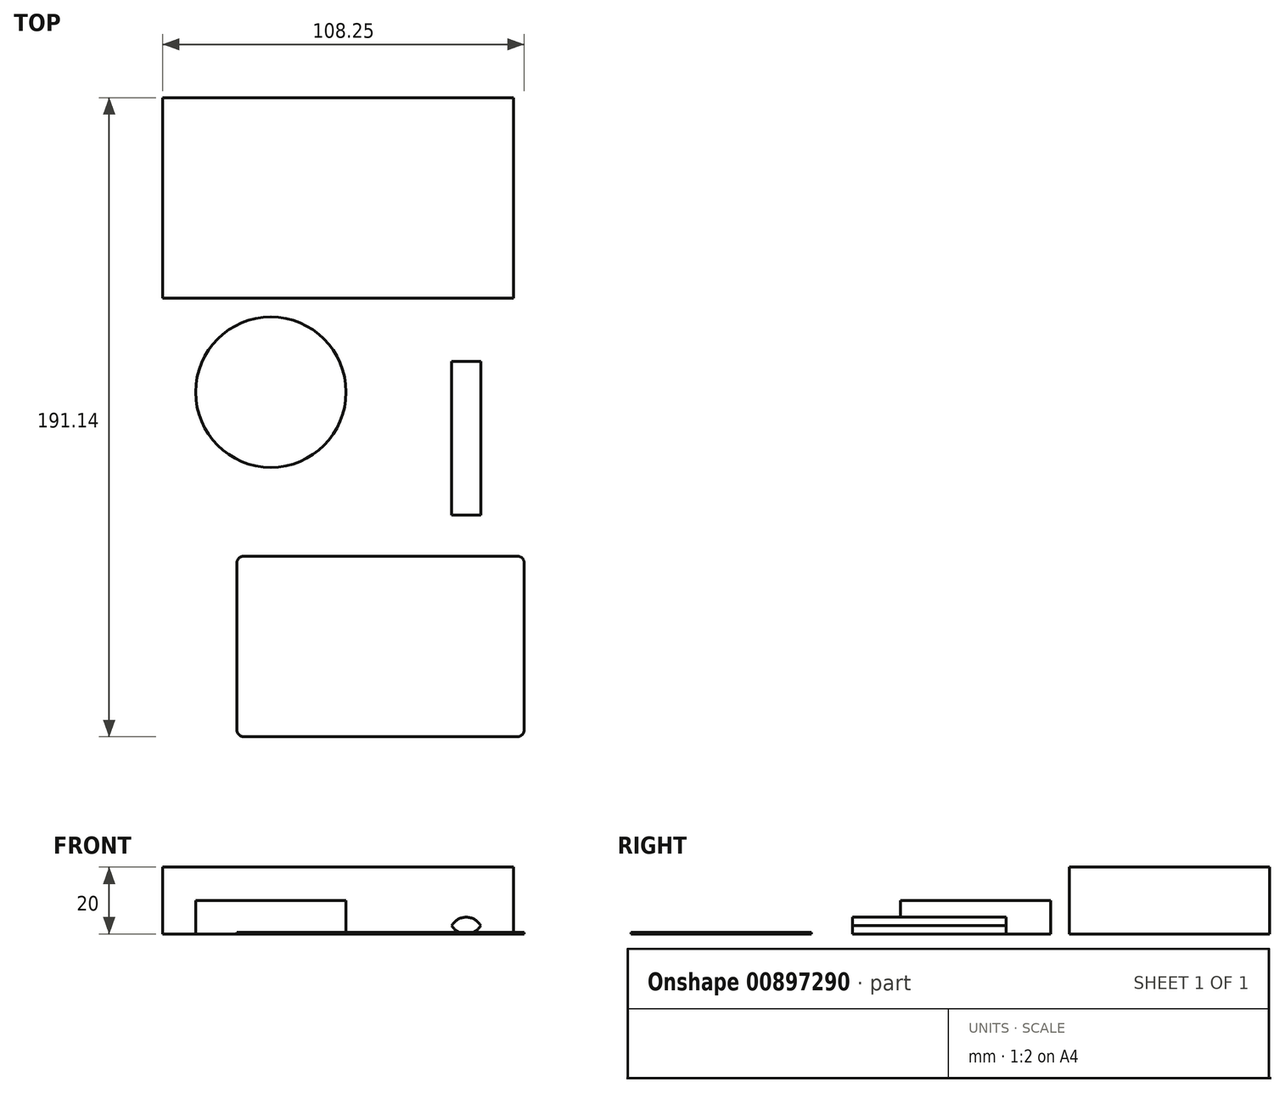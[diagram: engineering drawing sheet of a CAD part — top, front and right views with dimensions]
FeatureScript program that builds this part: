
annotation { "Feature Type Name" : "Feature", "Feature Type Description" : "" }
export const myFeature = defineFeature(function(context is Context, id is Id, definition is map)
    precondition{}
    {
        {
            var Q0;
            Q0=qCreatedBy(makeId("Top.planeOp"),FACE);
            var sketch = newSketch(context, id + "F0", { "sketchPlane" : qUnion([Q0])});
            skLineSegment(sketch, "E0.bottom", {"start": v(0, 0) * mm, "end": v(105, 0) * mm});
            skLineSegment(sketch, "E0.top", {"start": v(0, 60) * mm, "end": v(105, 60) * mm});
            skLineSegment(sketch, "E0.left", {"start": v(0, 0) * mm, "end": v(0, 60) * mm});
            skLineSegment(sketch, "E0.right", {"start": v(105, 0) * mm, "end": v(105, 60) * mm});
            skSolve(sketch);
        }
        {
            var Q0;
            Q0 = qSketchRegion(id + "F0", true);
            extrude(context, id + "F1", {"entities" : qUnion([Q0]), "depth" : 20 * mm, "offsetDistance" : 25 * mm});
        }
        {
            var Q0;
            Q0=qCreatedBy(makeId("Top.planeOp"),FACE);
            var sketch = newSketch(context, id + "F2", { "sketchPlane" : qUnion([Q0])});
            skCircle(sketch, "E1", {"center": v(32.4, -28.06) * mm, "radius": 22.5 * mm});
            skSolve(sketch);
        }
        {
            var Q0;
            Q0 = qSketchRegion(id + "F2", true);
            extrude(context, id + "F3", {"entities" : qUnion([Q0]), "depth" : 10 * mm, "offsetDistance" : 25 * mm});
        }
        {
            var Q0;
            Q0=qCreatedBy(makeId("Top.planeOp"),FACE);
            var sketch = newSketch(context, id + "F4", { "sketchPlane" : qUnion([Q0])});
            skLineSegment(sketch, "E2.bottom", {"start": v(24.25, -77.14) * mm, "end": v(106.25, -77.14) * mm});
            skLineSegment(sketch, "E2.top", {"start": v(24.25, -131.14) * mm, "end": v(106.25, -131.14) * mm});
            skLineSegment(sketch, "E2.left", {"start": v(22.25, -79.14) * mm, "end": v(22.25, -129.14) * mm});
            skLineSegment(sketch, "E2.right", {"start": v(108.25, -79.14) * mm, "end": v(108.25, -129.14) * mm});
            skPoint(sketch, "E3.visualSharp", {"position": v(108.25, -77.14) * mm});
            skArc(sketch, "E3.filletArc", {"start": v(108.25, -79.14) * mm, "mid": v(107.66, -77.73) * mm, "end": v(106.25, -77.14) * mm});
            skPoint(sketch, "E4.visualSharp", {"position": v(108.25, -131.14) * mm});
            skArc(sketch, "E4.filletArc", {"start": v(106.25, -131.14) * mm, "mid": v(107.66, -130.56) * mm, "end": v(108.25, -129.14) * mm});
            skPoint(sketch, "E5.visualSharp", {"position": v(22.25, -131.14) * mm});
            skArc(sketch, "E5.filletArc", {"start": v(22.25, -129.14) * mm, "mid": v(22.83, -130.56) * mm, "end": v(24.25, -131.14) * mm});
            skPoint(sketch, "E6.visualSharp", {"position": v(22.25, -77.14) * mm});
            skArc(sketch, "E6.filletArc", {"start": v(24.25, -77.14) * mm, "mid": v(22.83, -77.73) * mm, "end": v(22.25, -79.14) * mm});
            skSolve(sketch);
        }
        {
            var Q0;
            Q0 = qSketchRegion(id + "F4", true);
            extrude(context, id + "F5", {"entities" : qUnion([Q0]), "depth" : .4 * mm, "offsetDistance" : 25 * mm});
        }
        {
            var Q0;
            Q0=qCreatedBy(makeId("Top.planeOp"),FACE);
            var sketch = newSketch(context, id + "F6", { "sketchPlane" : qUnion([Q0])});
            skLineSegment(sketch, "E7.bottom", {"start": v(85.9, -18.83) * mm, "end": v(95.9, -18.83) * mm});
            skLineSegment(sketch, "E7.top", {"start": v(85.9, -64.83) * mm, "end": v(95.9, -64.83) * mm});
            skLineSegment(sketch, "E7.left", {"start": v(85.9, -18.83) * mm, "end": v(85.9, -64.83) * mm});
            skLineSegment(sketch, "E7.right", {"start": v(95.9, -18.83) * mm, "end": v(95.9, -64.83) * mm});
            skSolve(sketch);
        }
        {
            var Q0;
            Q0 = qSketchRegion(id + "F6", true);
            extrude(context, id + "F7", {"entities" : qUnion([Q0]), "depth" : 5 * mm, "offsetDistance" : 25 * mm});
        }
        {
            var Q0;
            Q0=makeQuery(id+"F7.opExtrude","CAP_EDGE",EDGE,{"disambiguationData":[OSD([sQuery(id+"F6.wireOp",EDGE,"E7.right")])],"isStart":true});
            var Q1;
            Q1=makeQuery(id+"F7.opExtrude","CAP_EDGE",EDGE,{"disambiguationData":[OSD([sQuery(id+"F6.wireOp",EDGE,"E7.left")])],"isStart":true});
            var Q2;
            Q2=makeQuery(id+"F7.opExtrude","CAP_EDGE",EDGE,{"disambiguationData":[OSD([sQuery(id+"F6.wireOp",EDGE,"E7.left")])],"isStart":false});
            var Q3;
            Q3=makeQuery(id+"F7.opExtrude","CAP_EDGE",EDGE,{"disambiguationData":[OSD([sQuery(id+"F6.wireOp",EDGE,"E7.right")])],"isStart":false});
            fillet(context, id + "F8", {"entities" : qUnion([Q0, Q1, Q2, Q3]), "radius" : 5 * mm, "tangentPropagation" : true, "allowEdgeOverflow" : false});
        }
    });
